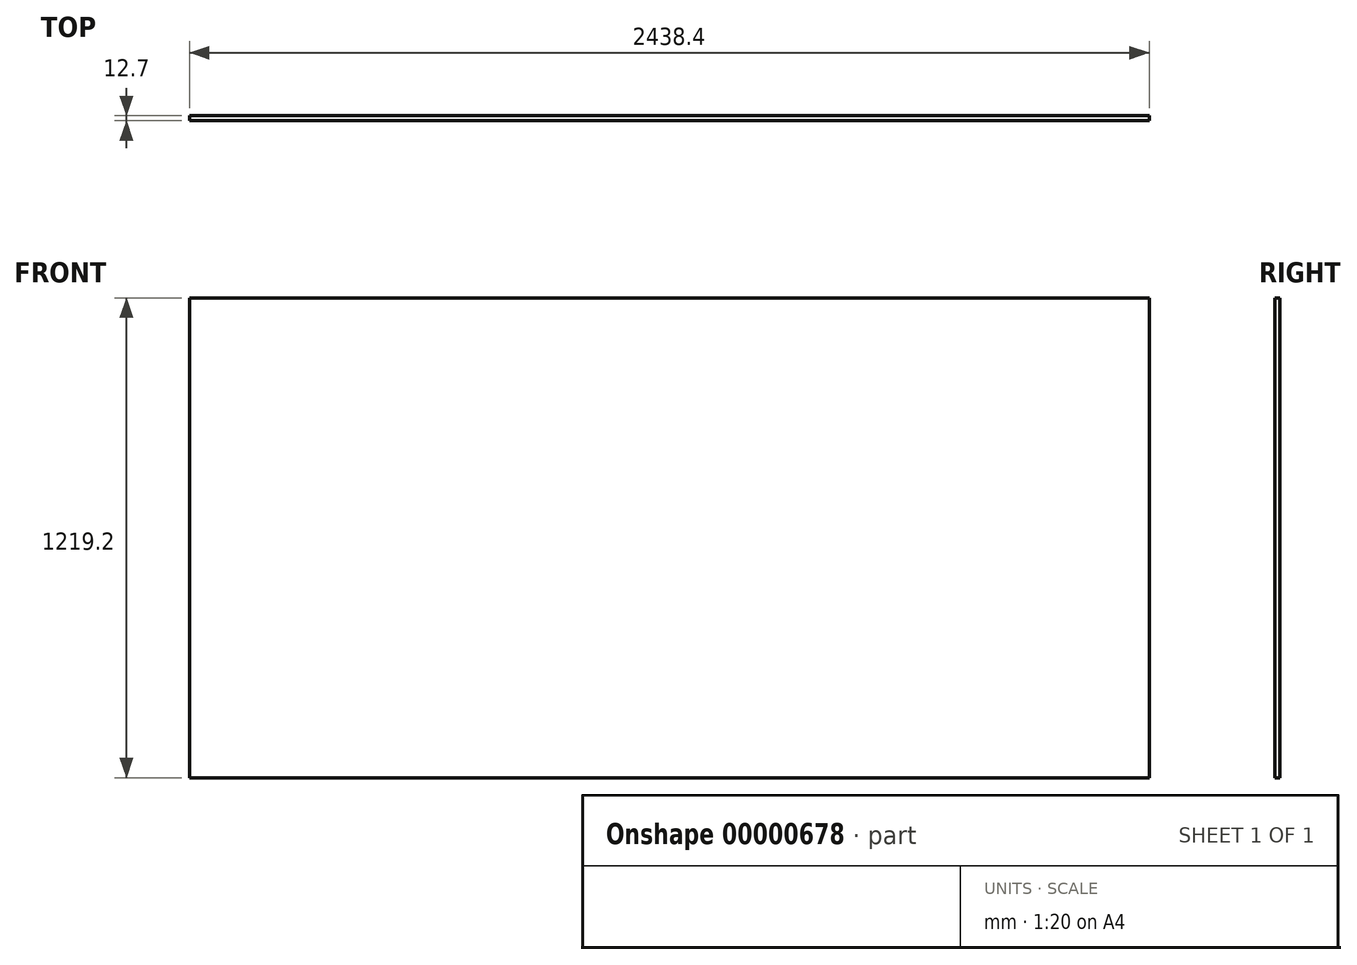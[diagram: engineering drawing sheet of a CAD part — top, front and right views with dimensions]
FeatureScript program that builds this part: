
annotation { "Feature Type Name" : "Feature", "Feature Type Description" : "" }
export const myFeature = defineFeature(function(context is Context, id is Id, definition is map)
    precondition{}
    {
        {
            var Q0;
            Q0=qCreatedBy(makeId("Front.planeOp"),FACE);
            var sketch = newSketch(context, id + "F0", { "sketchPlane" : qUnion([Q0])});
            skLineSegment(sketch, "E0.bottom", {"start": v(0, 0) * mm, "end": v(2438.4, 0) * mm});
            skLineSegment(sketch, "E0.top", {"start": v(0, 1219.2) * mm, "end": v(2438.4, 1219.2) * mm});
            skLineSegment(sketch, "E0.left", {"start": v(0, 0) * mm, "end": v(0, 1219.2) * mm});
            skLineSegment(sketch, "E0.right", {"start": v(2438.4, 0) * mm, "end": v(2438.4, 1219.2) * mm});
            skSolve(sketch);
        }
        {
            var Q0;
            Q0=makeQuery(id+"F0.imprint","IMPRINT",FACE,{"disambiguationData":[TD([[makeQuery(id+"F0.imprint","IMPRINT",EDGE,{"derivedFrom":sQuery(id+"F0.wireOp",EDGE,"E0.bottom")}),1.0]])]});
            extrude(context, id + "F1", {"entities" : qUnion([Q0]), "depth" : 12.7 * mm});
        }
    });
